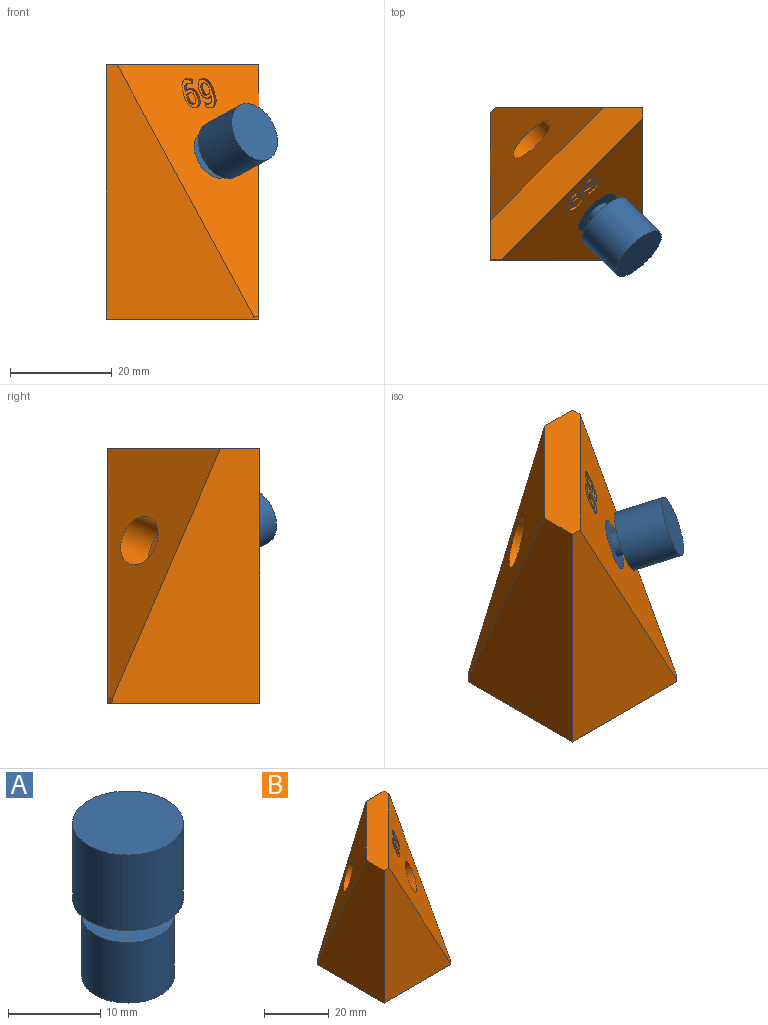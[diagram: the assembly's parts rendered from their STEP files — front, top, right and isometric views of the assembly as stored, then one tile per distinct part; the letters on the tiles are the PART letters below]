
ASSEMBLY  parts=2 mates=1
PART A: 7 faces, bbox 12x12x20.3 mm
  f0: cylinder r=5mm len=10mm, axis (0,0,-1), area 251.3mm2, adj f1,f2
  f1: plane 10x10mm, normal (0,0,1), area 58.9mm2, adj f0,f3
  f2: plane 10x10mm, normal (0,0,-1), area 78.5mm2, adj f0
  f3: cylinder r=2.5mm len=5mm, axis (0,0,-1), area 36.1mm2, adj f1,f6
  f4: cylinder r=6mm len=12mm, axis (0,0,-1), area 377mm2, adj f5,f6
  f5: plane 12x12mm, normal (0,0,1), area 113.1mm2, adj f4
  f6: plane 12x12mm, normal (0,0,-1), area 93.5mm2, adj f3,f4
PART B: 74 faces, bbox 30x30x50 mm
  f0: plane 50x29mm, normal (0,-1,0), area 785mm2, adj f3,f4,f5,f7,f8
  f1: plane 50x29mm, normal (1,0,0), area 785mm2, adj f2,f4,f5,f7,f8
  f2: plane 50x29mm, normal (0,1,0), area 929.6mm2, adj f1,f4,f5,f6,f9
  f3: plane 50x29mm, normal (-1,0,0), area 929.6mm2, adj f0,f4,f5,f6,f9
  f4: plane 30x30mm, normal (0,0,1), area 264.9mm2, adj f0,f1,f2,f3,f8,f9
  f5: plane 30x30mm, normal (0,0,-1), area 899mm2, adj f0,f1,f2,f3,f6,f7
  f6: plane 1x1mm, normal (-0.71,0.71,0), area 1.3mm2, adj f2,f3,f5,f9
  f7: plane 1x1mm, normal (0.71,-0.71,0), area 0.7mm2, adj f0,f1,f5,f8
  f8: plane 49.5x27.87mm, normal (0.66,-0.66,0.36), area 967.3mm2, adj f0,f1,f4,f7,f10,f14,f15,f16
  f9: plane 49.06x22.21mm, normal (-0.68,0.68,0.29), area 763.6mm2, adj f2,f3,f4,f6,f12
  f10: cylinder r=5mm len=12.79mm, axis (0.66,-0.66,0.36), area 251.3mm2, adj f8,f11
  f11: plane 9.34x7.51mm, normal (0.66,-0.66,0.36), area 78.5mm2, adj f10
  f12: cylinder r=5mm len=12.78mm, axis (-0.68,0.68,0.29), area 251.3mm2, adj f9,f13
  f13: plane 9.56x7.37mm, normal (-0.68,0.68,0.29), area 78.5mm2, adj f12
  f14: extruded ~0.76x0.73mm, area 0.3mm2, adj f8,f15,f41,f42
  f15: extruded ~0.75x0.67mm, area 0.3mm2, adj f8,f14,f16,f42
  f16: plane 0.99x0.64mm, normal (0.74,0.66,-0.14), area 0.4mm2, adj f8,f15,f17,f42
  f17: extruded ~0.81x0.72mm, area 0.3mm2, adj f8,f16,f18,f42
  f18: extruded ~0.8x0.77mm, area 0.3mm2, adj f8,f17,f19,f42
  f19: extruded ~1.65x1.32mm, area 0.9mm2, adj f8,f18,f20,f42
  f20: extruded ~1.88x1.23mm, area 1mm2, adj f8,f19,f21,f42
  f21: plane 1.4x0.67mm, normal (-0.71,-0.71,0), area 0.7mm2, adj f8,f20,f22,f42
  f22: extruded ~1.84x1.19mm, area 1mm2, adj f8,f21,f23,f42
  f23: extruded ~1.55x1.23mm, area 0.8mm2, adj f8,f22,f24,f42
  f24: extruded ~1.51x1.19mm, area 0.8mm2, adj f8,f23,f25,f42
  f25: extruded ~1.61x1.12mm, area 0.8mm2, adj f8,f24,f26,f42
  f26: extruded ~1.6x1.06mm, area 0.8mm2, adj f8,f25,f27,f42
  f27: extruded ~1.4x1.13mm, area 0.7mm2, adj f8,f26,f28,f42
  f28: extruded ~0.79x0.72mm, area 0.3mm2, adj f8,f27,f29,f42
  f29: extruded ~0.77x0.57mm, area 0.3mm2, adj f8,f28,f30,f42
  f30: plane 0.35x0.35mm, normal (0.71,0.71,0), area 0mm2, adj f8,f29,f31,f42
  f31: extruded ~1.21x0.82mm, area 0.6mm2, adj f8,f30,f41,f42
  f32: extruded ~0.83x0.67mm, area 0.4mm2, adj f33,f40,f42,f43
  f33: extruded ~0.99x0.7mm, area 0.5mm2, adj f32,f34,f42,f43
  f34: extruded ~0.98x0.71mm, area 0.5mm2, adj f33,f35,f42,f43
  f35: extruded ~0.84x0.66mm, area 0.4mm2, adj f34,f36,f42,f43
  f36: extruded ~0.86x0.69mm, area 0.4mm2, adj f35,f37,f42,f43
  f37: extruded ~1.11x0.75mm, area 0.5mm2, adj f36,f38,f42,f43
  f38: plane 0.78x0.5mm, normal (0.71,0.71,0), area 0.3mm2, adj f37,f39,f42,f43
  f39: extruded ~0.66x0.5mm, area 0.2mm2, adj f38,f40,f42,f43
  f40: extruded ~0.73x0.67mm, area 0.3mm2, adj f32,f39,f42,f43
  f41: extruded ~0.97x0.78mm, area 0.4mm2, adj f8,f14,f31,f42
  f42: plane 5.77x3.69mm, normal (0.66,-0.66,0.36), area 14.9mm2, adj f14,f15,f16,f17,f18,f19,f20,f21
  f43: plane 2.25x1.49mm, normal (0.66,-0.66,0.36), area 3.3mm2, adj f32,f33,f34,f35,f36,f37,f38,f39
  f44: extruded ~1.73x1.37mm, area 1mm2, adj f8,f45,f71,f72
  f45: extruded ~2.03x1.3mm, area 1.1mm2, adj f8,f44,f46,f72
  f46: plane 1.16x0.6mm, normal (0.71,0.71,0), area 0.5mm2, adj f8,f45,f47,f72
  f47: extruded ~1.84x1.21mm, area 1mm2, adj f8,f46,f48,f72
  f48: extruded ~1.59x1.26mm, area 0.9mm2, adj f8,f47,f49,f72
  f49: extruded ~1.51x1.21mm, area 0.8mm2, adj f8,f48,f50,f72
  f50: extruded ~1.58x1.1mm, area 0.8mm2, adj f8,f49,f51,f72
  f51: extruded ~1.54x1.03mm, area 0.8mm2, adj f8,f50,f52,f72
  f52: extruded ~1.37x1.08mm, area 0.7mm2, adj f8,f51,f53,f72
  f53: extruded ~0.85x0.79mm, area 0.4mm2, adj f8,f52,f54,f72
  f54: extruded ~0.78x0.61mm, area 0.3mm2, adj f8,f53,f55,f72
  f55: plane 0.34x0.33mm, normal (-0.47,-0.74,-0.48), area 0mm2, adj f8,f54,f56,f72
  f56: extruded ~1.26x0.85mm, area 0.6mm2, adj f8,f55,f57,f72
  f57: extruded ~1.04x0.84mm, area 0.5mm2, adj f8,f56,f58,f72
  f58: extruded ~0.7x0.67mm, area 0.3mm2, adj f8,f57,f59,f72
  f59: extruded ~0.7x0.63mm, area 0.2mm2, adj f8,f58,f60,f72
  f60: plane 1x0.7mm, normal (-0.75,-0.63,0.21), area 0.5mm2, adj f8,f59,f61,f72
  f61: extruded ~0.78x0.69mm, area 0.3mm2, adj f8,f60,f71,f72
  f62: extruded ~0.84x0.68mm, area 0.4mm2, adj f63,f70,f72,f73
  f63: extruded ~0.93x0.7mm, area 0.4mm2, adj f62,f64,f72,f73
  f64: extruded ~0.95x0.69mm, area 0.4mm2, adj f63,f65,f72,f73
  f65: extruded ~0.84x0.66mm, area 0.4mm2, adj f64,f66,f72,f73
  f66: extruded ~0.91x0.72mm, area 0.4mm2, adj f65,f67,f72,f73
  f67: extruded ~1.2x0.79mm, area 0.6mm2, adj f66,f68,f72,f73
  f68: plane 0.55x0.43mm, normal (-0.71,-0.71,0), area 0.2mm2, adj f67,f69,f72,f73
  f69: extruded ~0.66x0.51mm, area 0.2mm2, adj f68,f70,f72,f73
  f70: extruded ~0.76x0.7mm, area 0.3mm2, adj f62,f69,f72,f73
  f71: extruded ~0.79x0.76mm, area 0.3mm2, adj f8,f44,f61,f72
  f72: plane 5.77x3.73mm, normal (0.66,-0.66,0.36), area 15mm2, adj f44,f45,f46,f47,f48,f49,f50,f51
  f73: plane 2.13x1.53mm, normal (0.66,-0.66,0.36), area 3.3mm2, adj f62,f63,f64,f65,f66,f67,f68,f69
PLACE A rot(axis=(0.8,0.51,0.3),72.9deg) t=(-1.67,10.57,23.05)mm
PLACE B t=(-2.42,10.95,-6.48)mm
MATE fastened A.f0 <-> B.f10  axis (-0.66,0.66,-0.36) through (-1.67,10.57,23.05)mm
